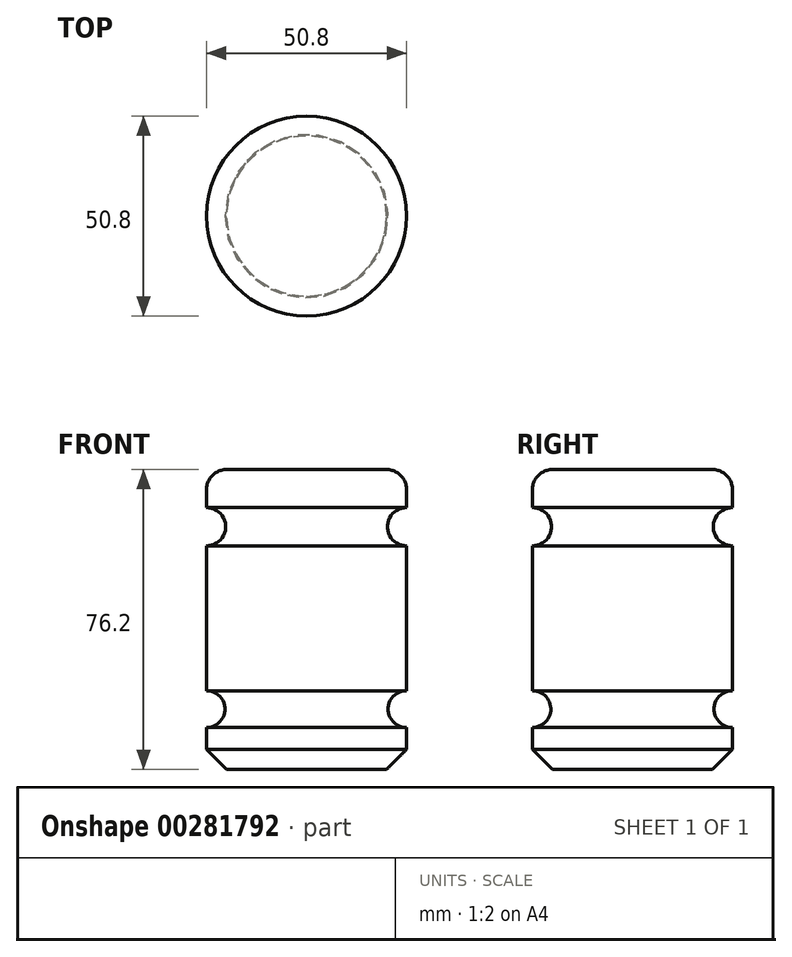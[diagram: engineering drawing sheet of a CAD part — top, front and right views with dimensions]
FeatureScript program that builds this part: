
annotation { "Feature Type Name" : "Feature", "Feature Type Description" : "" }
export const myFeature = defineFeature(function(context is Context, id is Id, definition is map)
    precondition{}
    {
        {
            var Q0;
            Q0=qCreatedBy(makeId("Front.planeOp"),FACE);
            var sketch = newSketch(context, id + "F0", { "sketchPlane" : qUnion([Q0])});
            skLineSegment(sketch, "E0.bottom", {"start": v(0, 0) * mm, "end": v(-25.4, 0) * mm});
            skLineSegment(sketch, "E0.top", {"start": v(0, 76.2) * mm, "end": v(-25.4, 76.2) * mm});
            skLineSegment(sketch, "E0.left", {"start": v(0, 0) * mm, "end": v(0, 10.67) * mm});
            skLineSegment(sketch, "E0.right", {"start": v(-25.4, 0) * mm, "end": v(-25.4, 76.2) * mm});
            skArc(sketch, "E1", {"start": v(0, 66.52) * mm, "mid": v(-4.86, 61.66) * mm, "end": v(0, 56.8) * mm});
            skArc(sketch, "E2", {"start": v(0, 20) * mm, "mid": v(-4.67, 15.34) * mm, "end": v(0, 10.67) * mm});
            skLineSegment(sketch, "E3.trimOffspring", {"start": v(0, 20) * mm, "end": v(0, 56.8) * mm});
            skLineSegment(sketch, "E4.trimOffspring", {"start": v(0, 66.52) * mm, "end": v(0, 76.2) * mm});
            skSolve(sketch);
        }
        {
            var Q0;
            Q0 = qSketchRegion(id + "F0", true);
            var Q1;
            Q1=sQuery(id+"F0.wireOp",EDGE,"E0.right");
            revolve(context, id + "F1", {"entities" : qUnion([Q0]), "axis" : qUnion([Q1]), "revolveType" : RevolveType.FULL});
        }
        {
            var Q0;
            Q0=makeQuery(id+"F1.opRevolve","SWEPT_FACE",FACE,{"disambiguationData":[OSD([sQuery(id+"F0.wireOp",EDGE,"E0.top")])]});
            fillet(context, id + "F2", {"entities" : qUnion([Q0]), "radius" : 5.08 * mm, "tangentPropagation" : true, "allowEdgeOverflow" : false});
        }
        {
            var Q0;
            Q0=makeQuery(id+"F1.opRevolve","SWEPT_EDGE",EDGE,{"disambiguationData":[OSD([sQuery(id+"F0.wireOp",EDGE,"E0.bottom"),sQuery(id+"F0.wireOp",EDGE,"E0.left")])]});
            chamfer(context, id + "F3", {"entities" : qUnion([Q0]), "width" : 5.08 * mm, "tangentPropagation" : true});
        }
    });
